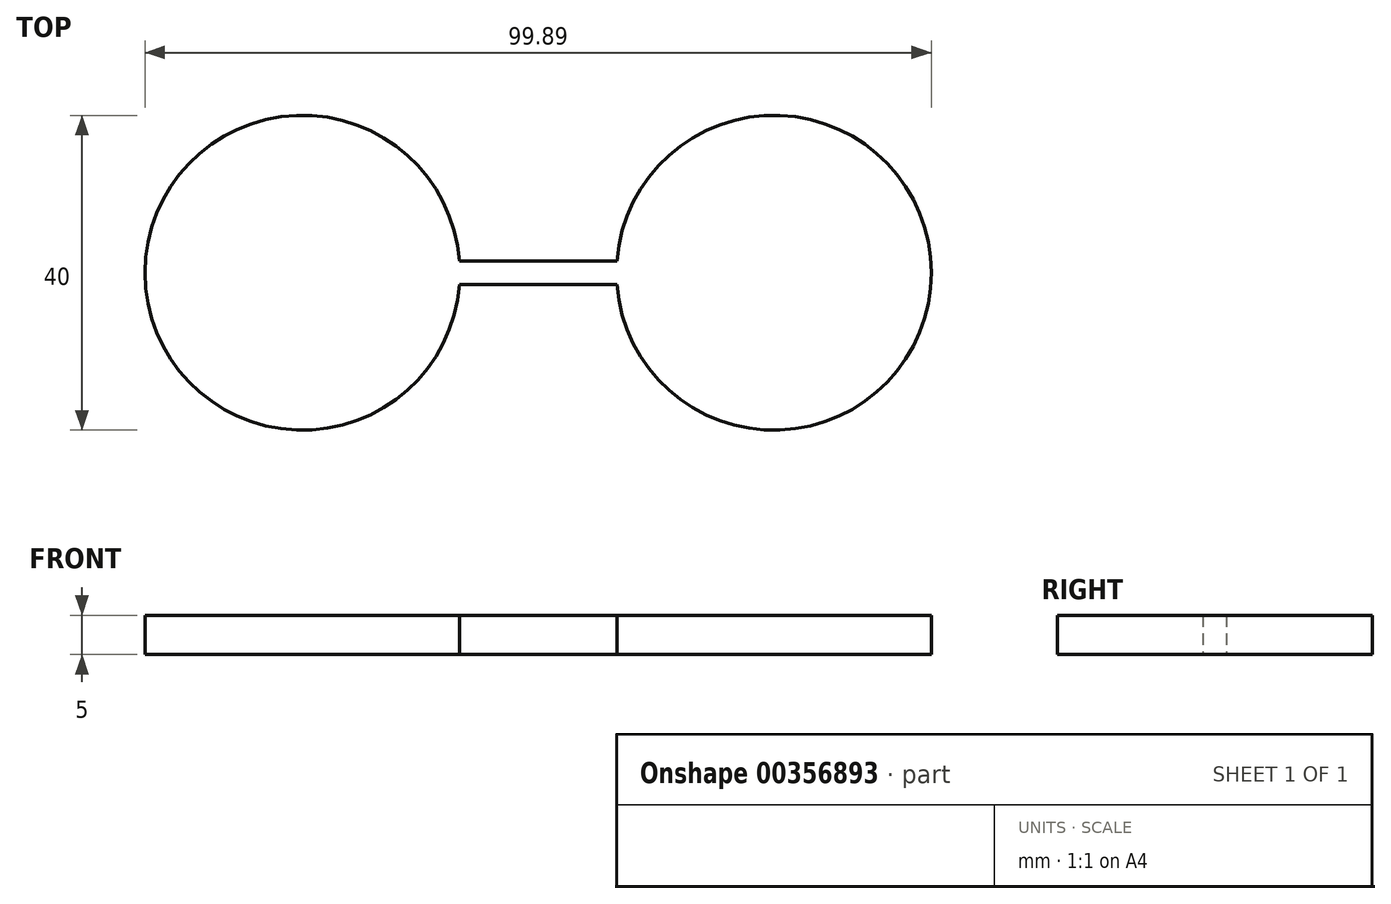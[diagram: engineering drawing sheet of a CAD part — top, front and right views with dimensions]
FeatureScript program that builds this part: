
annotation { "Feature Type Name" : "Feature", "Feature Type Description" : "" }
export const myFeature = defineFeature(function(context is Context, id is Id, definition is map)
    precondition{}
    {
        {
            var Q0;
            Q0=qCreatedBy(makeId("Top.planeOp"),FACE);
            var sketch = newSketch(context, id + "F0", { "sketchPlane" : qUnion([Q0])});
            skLineSegment(sketch, "E0", {"start": v(37.84, 2.87) * mm, "end": v(57.84, 2.87) * mm});
            skLineSegment(sketch, "E1", {"start": v(57.84, -0.13) * mm, "end": v(37.84, -0.13) * mm});
            skArc(sketch, "E2", {"start": v(57.84, -0.13) * mm, "mid": v(97.78, 1.37) * mm, "end": v(57.84, 2.87) * mm});
            skArc(sketch, "E3", {"start": v(37.84, 2.87) * mm, "mid": v(-2.1, 1.37) * mm, "end": v(37.84, -0.13) * mm});
            skSolve(sketch);
        }
        {
            var Q0;
            Q0=makeQuery(id+"F0.imprint","IMPRINT",FACE,{"disambiguationData":[TD([[makeQuery(id+"F0.imprint","IMPRINT",EDGE,{"derivedFrom":sQuery(id+"F0.wireOp",EDGE,"E0")}),-1.0]])]});
            extrude(context, id + "F1", {"entities" : qUnion([Q0]), "offsetDistance" : 25 * mm, "depth" : 5 * mm});
        }
    });
